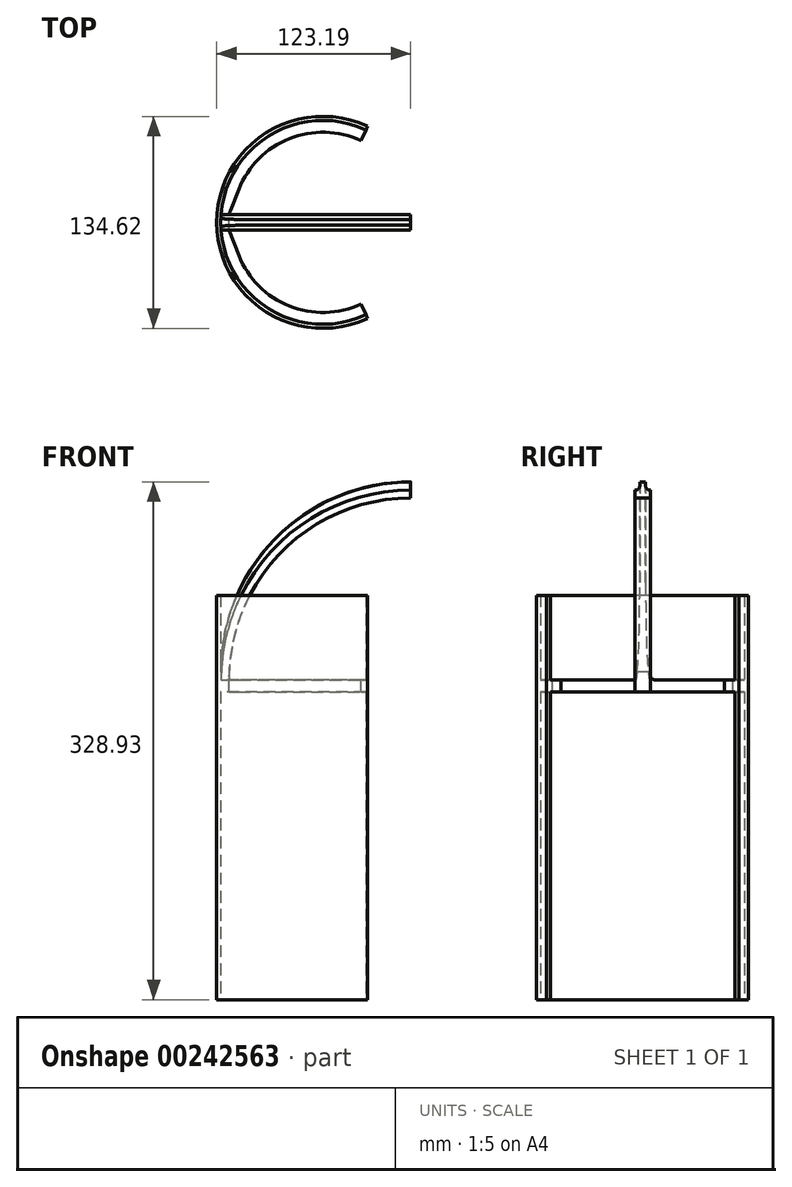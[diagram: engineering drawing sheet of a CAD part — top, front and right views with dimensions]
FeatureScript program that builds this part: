
annotation { "Feature Type Name" : "Feature", "Feature Type Description" : "" }
export const myFeature = defineFeature(function(context is Context, id is Id, definition is map)
    precondition{}
    {
        {
            var Q0;
            Q0=qCreatedBy(makeId("Top.planeOp"),FACE);
            var sketch = newSketch(context, id + "F0", { "sketchPlane" : qUnion([Q0])});
            skLineSegment(sketch, "E0.bottom", {"start": v(0, 5) * mm, "end": v(-31.75, 5) * mm});
            skLineSegment(sketch, "E0.top", {"start": v(0, -5) * mm, "end": v(-31.75, -5) * mm});
            skLineSegment(sketch, "E0.left", {"start": v(0, 5) * mm, "end": v(0, -5) * mm});
            skLineSegment(sketch, "E0.right", {"start": v(-31.75, 5) * mm, "end": v(-31.75, -5) * mm});
            skCircle(sketch, "E1", {"center": v(-55.88, 0) * mm, "radius": 64.77 * mm});
            skLineSegment(sketch, "E2", {"start": v(-55.88, 0) * mm, "end": v(-28.5, 58.7) * mm});
            skLineSegment(sketch, "E3", {"start": v(-55.88, 0) * mm, "end": v(-28.5, -58.7) * mm});
            skCircle(sketch, "E4", {"center": v(-55.88, 0) * mm, "radius": 57.27 * mm});
            skLineSegment(sketch, "E5.bottom", {"start": v(-120.46, -5) * mm, "end": v(-95, -5) * mm});
            skLineSegment(sketch, "E5.top", {"start": v(-120.46, 5) * mm, "end": v(-95, 5) * mm});
            skLineSegment(sketch, "E5.left", {"start": v(-120.46, -5) * mm, "end": v(-120.46, 5) * mm});
            skLineSegment(sketch, "E5.right", {"start": v(-95, -5) * mm, "end": v(-95, 5) * mm});
            skPoint(sketch, "E5.middle", {"position": v(-107.73, 0) * mm});
            skLineSegment(sketch, "E6.bottom", {"start": v(-112.93, -5) * mm, "end": v(-115.47, -5) * mm});
            skLineSegment(sketch, "E6.top", {"start": v(-112.93, 5) * mm, "end": v(-115.47, 5) * mm});
            skLineSegment(sketch, "E6.left", {"start": v(-112.93, -5) * mm, "end": v(-112.93, 5) * mm});
            skLineSegment(sketch, "E6.right", {"start": v(-115.47, -5) * mm, "end": v(-115.47, 5) * mm});
            skLineSegment(sketch, "E7", {"start": v(-115.47, -5) * mm, "end": v(-109.16, -21.01) * mm});
            skLineSegment(sketch, "E8", {"start": v(-115.47, 5) * mm, "end": v(-109.16, 21.01) * mm});
            skSolve(sketch);
        }
        {
            var Q0;
            {var subQ0=sQuery(id+"F0.wireOp",EDGE,"E5.left");Q0=makeQuery(id+"F0.imprint","IMPRINT",FACE,{"disambiguationData":[TD([[makeQuery(id+"F0.imprint","IMPRINT",EDGE,{"derivedFrom":subQ0}),1.0]])]});}
            var Q1;
            {var subQ0=sQuery(id+"F0.wireOp",EDGE,"E2");var subQ1=sQuery(id+"F0.wireOp",EDGE,"E1");var subQ2=makeQuery(id+"F0.imprint","INTERSECT",VERTEX,{"derivedFrom":[subQ1,subQ0]});Q1=makeQuery(id+"F0.imprint","IMPRINT",FACE,{"disambiguationData":[TD([[makeQuery(id+"F0.imprint","IMPRINT",EDGE,{"disambiguationData":[TD([[subQ2,1.0]])],"derivedFrom":subQ0}),1.0]])]});}
            var Q2;
            {var subQ0=sQuery(id+"F0.wireOp",EDGE,"E3");var subQ1=sQuery(id+"F0.wireOp",EDGE,"E1");var subQ2=makeQuery(id+"F0.imprint","INTERSECT",VERTEX,{"derivedFrom":[subQ1,subQ0]});Q2=makeQuery(id+"F0.imprint","IMPRINT",FACE,{"disambiguationData":[TD([[makeQuery(id+"F0.imprint","IMPRINT",EDGE,{"disambiguationData":[TD([[subQ2,1.0]])],"derivedFrom":subQ0}),-1.0]])]});}
            var Q3;
            {var subQ5=sQuery(id+"F0.wireOp",EDGE,"E5.left");Q3=makeQuery(id+"F0.imprint","IMPRINT",FACE,{"disambiguationData":[TD([[makeQuery(id+"F0.imprint","IMPRINT",EDGE,{"derivedFrom":subQ5}),-1.0]])]});}
            var Q4;
            {var subQ0=sQuery(id+"F0.wireOp",EDGE,"E6.top");Q4=makeQuery(id+"F0.imprint","IMPRINT",FACE,{"disambiguationData":[TD([[makeQuery(id+"F0.imprint","IMPRINT",EDGE,{"derivedFrom":subQ0}),-1.0]])]});}
            var Q5;
            {var subQ1=sQuery(id+"F0.wireOp",EDGE,"E6.bottom");Q5=makeQuery(id+"F0.imprint","IMPRINT",FACE,{"disambiguationData":[TD([[makeQuery(id+"F0.imprint","IMPRINT",EDGE,{"derivedFrom":subQ1}),-1.0]])]});}
            var Q6;
            {var subQ0=sQuery(id+"F0.wireOp",EDGE,"E6.bottom");Q6=makeQuery(id+"F0.imprint","IMPRINT",FACE,{"disambiguationData":[TD([[makeQuery(id+"F0.imprint","IMPRINT",EDGE,{"derivedFrom":subQ0}),1.0]])]});}
            extrude(context, id + "F1", {"entities" : qUnion([Q0, Q1, Q2, Q3, Q4, Q5, Q6]), "oppositeDirection" : true, "depth" : 7.62 * mm});
        }
        {
            var Q0;
            {var subQ5=sQuery(id+"F0.wireOp",EDGE,"E5.left");Q0=makeQuery(id+"F0.imprint","IMPRINT",FACE,{"disambiguationData":[TD([[makeQuery(id+"F0.imprint","IMPRINT",EDGE,{"derivedFrom":subQ5}),-1.0]])]});}
            var Q1;
            {var subQ0=sQuery(id+"F0.wireOp",EDGE,"E5.left");Q1=makeQuery(id+"F0.imprint","IMPRINT",FACE,{"disambiguationData":[TD([[makeQuery(id+"F0.imprint","IMPRINT",EDGE,{"derivedFrom":subQ0}),1.0]])]});}
            var Q2;
            {var subQ1=sQuery(id+"F0.wireOp",EDGE,"E6.bottom");Q2=makeQuery(id+"F0.imprint","IMPRINT",FACE,{"disambiguationData":[TD([[makeQuery(id+"F0.imprint","IMPRINT",EDGE,{"derivedFrom":subQ1}),-1.0]])]});}
            var Q3;
            Q3=sQuery(id+"F0.wireOp",EDGE,"E0.left");
            revolve(context, id + "F2", {"operationType" : NewBodyOperationType.ADD, "entities" : qUnion([Q0, Q1, Q2]), "axis" : qUnion([Q3]), "revolveType" : RevolveType.ONE_DIRECTION, "oppositeDirection" : true, "angle" : 90 * degree});
        }
        {
            var Q0;
            Q0=qCreatedBy(makeId("Top.planeOp"),FACE);
            var sketch = newSketch(context, id + "F3", { "sketchPlane" : qUnion([Q0])});
            skArc(sketch, "E9.0", {"start": v(-122.93, -5.89) * mm, "mid": v(-89.53, -58.3) * mm, "end": v(-27.43, -61) * mm});
            skArc(sketch, "E9.1", {"start": v(-122.93, 5.89) * mm, "mid": v(-123.2, 0) * mm, "end": v(-122.93, -5.89) * mm});
            skArc(sketch, "E9.2", {"start": v(-27.43, 61) * mm, "mid": v(-89.53, 58.3) * mm, "end": v(-122.93, 5.89) * mm});
            skArc(sketch, "E10.0", {"start": v(-28.5, 58.7) * mm, "mid": v(-88.54, 55.93) * mm, "end": v(-120.46, 5) * mm});
            skArc(sketch, "E11.0", {"start": v(-120.46, 5) * mm, "mid": v(-120.65, 0) * mm, "end": v(-120.46, -5) * mm});
            skArc(sketch, "E12.0", {"start": v(-120.46, -5) * mm, "mid": v(-88.54, -55.93) * mm, "end": v(-28.5, -58.7) * mm});
            skLineSegment(sketch, "E13", {"start": v(-28.5, 58.7) * mm, "end": v(-27.43, 61) * mm});
            skLineSegment(sketch, "E14", {"start": v(-28.5, -58.7) * mm, "end": v(-27.43, -61) * mm});
            skSolve(sketch);
        }
        {
            var Q0;
            Q0=qSketchRegion(id+"F3",true);
            extrude(context, id + "F4", {"entities" : qUnion([Q0]), "depth" : 53.6 * mm});
        }
        {
            var Q0;
            Q0=makeQuery(id+"F4.opExtrude","CAP_FACE",FACE,{"disambiguationData":[OSD([sQuery(id+"F3.wireOp",EDGE,"E9.0"),sQuery(id+"F3.wireOp",EDGE,"E9.1"),sQuery(id+"F3.wireOp",EDGE,"E9.2"),sQuery(id+"F3.wireOp",EDGE,"E10.0"),sQuery(id+"F3.wireOp",EDGE,"E11.0"),sQuery(id+"F3.wireOp",EDGE,"E12.0"),sQuery(id+"F3.wireOp",EDGE,"E13"),sQuery(id+"F3.wireOp",EDGE,"E14")])],"isStart":true});
            extrude(context, id + "F5", {"entities" : qUnion([Q0]), "operationType" : NewBodyOperationType.ADD, "depth" : 203.2 * mm});
        }
        {
            var Q0;
            Q0=qCreatedBy(makeId("Top.planeOp"),FACE);
            var sketch = newSketch(context, id + "F6", { "sketchPlane" : qUnion([Q0])});
            skLineSegment(sketch, "E15.bottom", {"start": v(-120.62, -1.85) * mm, "end": v(-115.47, -1.85) * mm});
            skLineSegment(sketch, "E15.top", {"start": v(-120.62, 1.85) * mm, "end": v(-115.47, 1.85) * mm});
            skLineSegment(sketch, "E15.left", {"start": v(-120.62, -1.85) * mm, "end": v(-120.62, 1.85) * mm});
            skLineSegment(sketch, "E15.right", {"start": v(-115.47, -1.85) * mm, "end": v(-115.47, 1.85) * mm});
            skPoint(sketch, "E15.middle", {"position": v(-118.05, 0) * mm});
            skCircle(sketch, "E16.0", {"center": v(-55.88, 0) * mm, "radius": 64.77 * mm});
            skCircle(sketch, "E17.0", {"center": v(-55.88, 0) * mm, "radius": 57.27 * mm});
            skLineSegment(sketch, "E18.0", {"start": v(-115.47, -5) * mm, "end": v(-115.47, 5) * mm});
            skSolve(sketch);
        }
        {
            var Q0;
            {var subQ0=sQuery(id+"F6.wireOp",EDGE,"E15.bottom");Q0=makeQuery(id+"F6.imprint","IMPRINT",FACE,{"disambiguationData":[TD([[makeQuery(id+"F6.imprint","IMPRINT",EDGE,{"derivedFrom":subQ0}),1.0]])]});}
            var Q1;
            {var subQ0=sQuery(id+"F6.wireOp",EDGE,"E15.left");Q1=makeQuery(id+"F6.imprint","IMPRINT",FACE,{"disambiguationData":[TD([[makeQuery(id+"F6.imprint","IMPRINT",EDGE,{"derivedFrom":subQ0}),1.0]])]});}
            var Q2;
            Q2=sQuery(id+"F0.wireOp",EDGE,"E0.left");
            revolve(context, id + "F7", {"entities" : qUnion([Q0, Q1]), "axis" : qUnion([Q2]), "revolveType" : RevolveType.ONE_DIRECTION, "oppositeDirection" : true, "angle" : 90 * degree});
        }
        {
            var Q0;
            Q0=makeQuery(id+"F7.opRevolve","SWEPT_BODY",BODY,{"disambiguationData":[OSD([sQuery(id+"F6.wireOp",EDGE,"E15.bottom"),sQuery(id+"F6.wireOp",EDGE,"E15.top"),sQuery(id+"F6.wireOp",EDGE,"E16.0"),sQuery(id+"F6.wireOp",EDGE,"E18.0")])]});
            var Q1;
            {var subQ0=sQuery(id+"F3.wireOp",EDGE,"E14");var subQ1=sQuery(id+"F3.wireOp",EDGE,"E9.0");Q1=makeQuery(id+"F5.boolean.opBoolean","MERGE",EDGE,{"derivedFrom":[makeQuery(id+"F4.opExtrude","SWEPT_EDGE",EDGE,{"disambiguationData":[OSD([subQ1,subQ0])]}),makeQuery(id+"F5.opExtrude","SWEPT_EDGE",EDGE,{"disambiguationData":[OSD([subQ1,subQ0])]})]});}
            transform(context, id + "F8", {"entities" : qUnion([Q0]), "transformType" : TransformType.TRANSLATION_3D, "dx" : 0 * mm, "dy" : 0 * mm, "dz" : 5.08 * mm, "makeCopy" : false});
        }
        {
            var Q0;
            Q0=makeQuery(id+"F7.opRevolve","CAP_FACE",FACE,{"disambiguationData":[OSD([sQuery(id+"F6.wireOp",EDGE,"E15.bottom"),sQuery(id+"F6.wireOp",EDGE,"E15.top"),sQuery(id+"F6.wireOp",EDGE,"E16.0"),sQuery(id+"F6.wireOp",EDGE,"E18.0")])],"isStart":true});
            extrude(context, id + "F9", {"entities" : qUnion([Q0]), "operationType" : NewBodyOperationType.ADD, "depth" : 10.26 * mm});
        }
        {
            var Q0;
            Q0=makeQuery(id+"F2.opRevolve","CAP_EDGE",EDGE,{"disambiguationData":[OSD([sQuery(id+"F0.wireOp",EDGE,"E5.top")])],"isStart":true});
            var Q1;
            Q1=makeQuery(id+"F2.opRevolve","CAP_EDGE",EDGE,{"disambiguationData":[OSD([sQuery(id+"F0.wireOp",EDGE,"E5.bottom")])],"isStart":true});
            var Q2;
            Q2=makeQuery(id+"F9.boolean.opBoolean","INTERSECT",EDGE,{"derivedFrom":[makeQuery(id+"F2.opRevolve","SWEPT_FACE",FACE,{"disambiguationData":[OSD([sQuery(id+"F0.wireOp",EDGE,"E1")])]}),makeQuery(id+"F9.opExtrude","SWEPT_FACE",FACE,{"disambiguationData":[OSD([sQuery(id+"F6.wireOp",EDGE,"E15.bottom")])]})]});
            var Q3;
            Q3=makeQuery(id+"F9.boolean.opBoolean","INTERSECT",EDGE,{"derivedFrom":[makeQuery(id+"F2.opRevolve","SWEPT_FACE",FACE,{"disambiguationData":[OSD([sQuery(id+"F0.wireOp",EDGE,"E1")])]}),makeQuery(id+"F9.opExtrude","SWEPT_FACE",FACE,{"disambiguationData":[OSD([sQuery(id+"F6.wireOp",EDGE,"E15.top")])]})]});
            fillet(context, id + "F10", {"entities" : qUnion([Q0, Q1, Q2, Q3]), "radius" : 2.6 * mm, "tangentPropagation" : true, "allowEdgeOverflow" : false});
        }
    });
